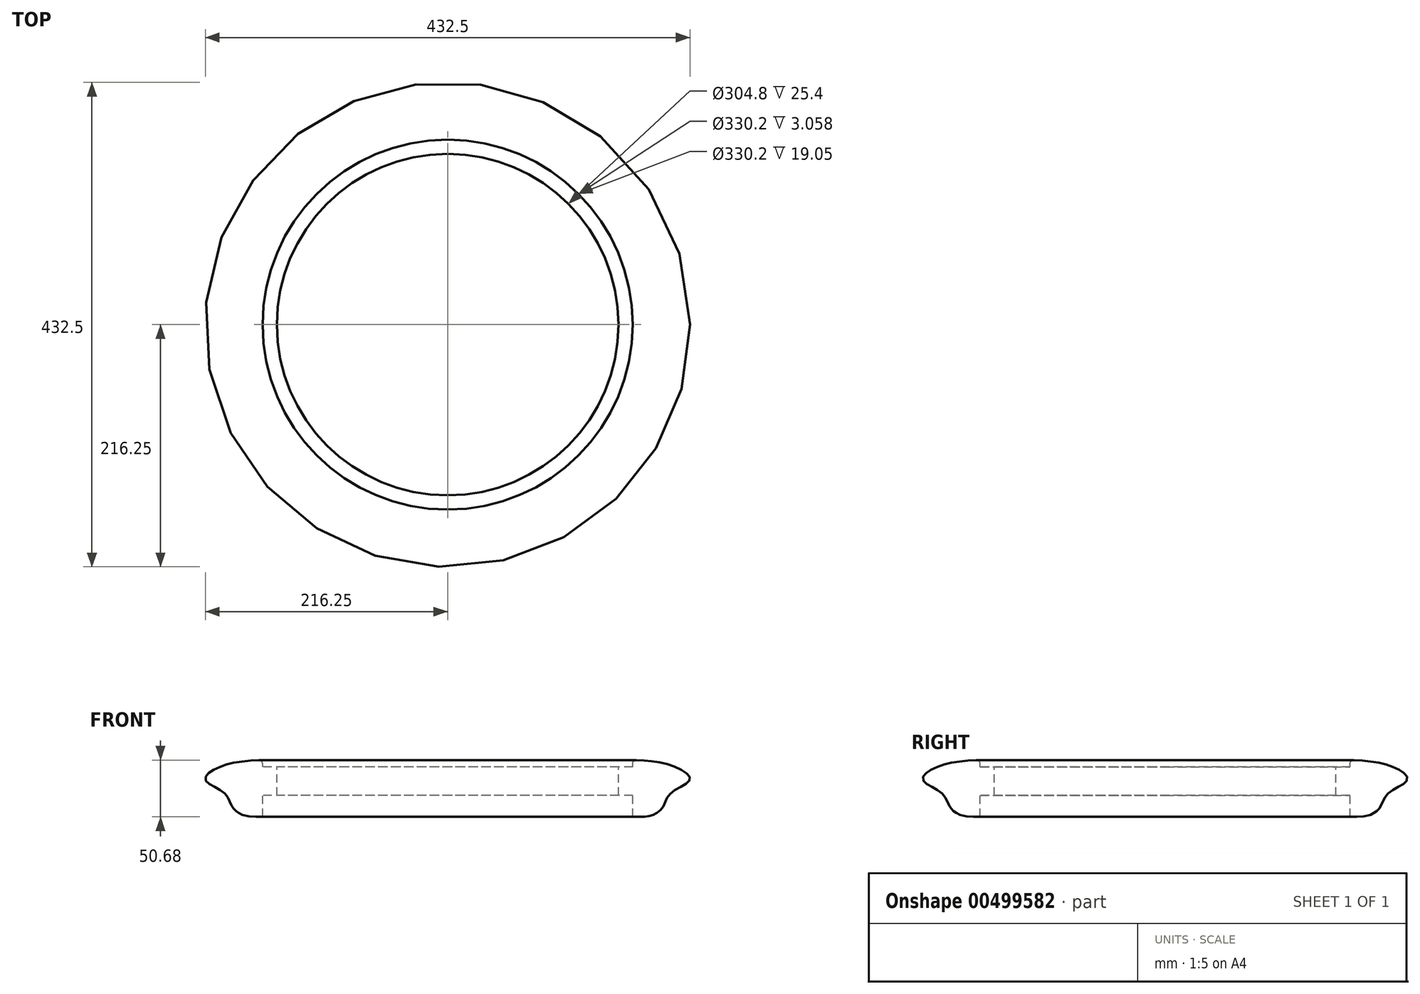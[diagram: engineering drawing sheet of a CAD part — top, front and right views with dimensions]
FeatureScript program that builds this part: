
annotation { "Feature Type Name" : "Feature", "Feature Type Description" : "" }
export const myFeature = defineFeature(function(context is Context, id is Id, definition is map)
    precondition{}
    {
        {
            var Q0;
            Q0=qCreatedBy(makeId("Front.planeOp"),FACE);
            var sketch = newSketch(context, id + "F0", { "sketchPlane" : qUnion([Q0])});
            skLineSegment(sketch, "E0", {"start": v(0, 33.86) * mm, "end": v(0, -42.34) * mm, "construction": true});
            skLineSegment(sketch, "E1", {"start": v(0, 0) * mm, "end": v(-152.4, 0) * mm, "construction": true});
            skSolve(sketch);
        }
        {
            var Q0;
            Q0=qCreatedBy(makeId("Front.planeOp"),FACE);
            var sketch = newSketch(context, id + "F1", { "sketchPlane" : qUnion([Q0])});
            skLineSegment(sketch, "E2", {"start": v(-152.4, 0) * mm, "end": v(-152.4, 25.4) * mm});
            skLineSegment(sketch, "E3", {"start": v(-152.4, 0) * mm, "end": v(-165.1, 0) * mm});
            skLineSegment(sketch, "E4", {"start": v(-152.4, 25.4) * mm, "end": v(-165.1, 25.4) * mm});
            skLineSegment(sketch, "E5", {"start": v(-165.1, 0) * mm, "end": v(-165.1, -19.05) * mm});
            skLineSegment(sketch, "E6", {"start": v(-165.1, 25.4) * mm, "end": v(-165.1, 31.75) * mm});
            skFitSpline(sketch, "E7", {"points": [v(-165.1, -19.05) * mm, v(-182.15, -17.64) * mm, v(-192.02, -10.3) * mm, v(-199.07, 2.01) * mm, v(-216.12, 14.15) * mm, v(-202.18, 25.95) * mm, v(-165.1, 31.75) * mm], "startDerivative": vector(-163.52, 1.27) * mm, "endDerivative": vector(153.64, 4.81) * mm});
            skSolve(sketch);
        }
        {
            var Q0;
            Q0=makeQuery(id+"F1.imprint","IMPRINT",FACE,{"disambiguationData":[TD([[makeQuery(id+"F1.imprint","IMPRINT",EDGE,{"derivedFrom":sQuery(id+"F1.wireOp",EDGE,"E2")}),1.0]])]});
            var Q1;
            Q1=sQuery(id+"F0.wireOp",EDGE,"E0");
            revolve(context, id + "F2", {"entities" : qUnion([Q0]), "axis" : qUnion([Q1]), "revolveType" : RevolveType.FULL});
        }
        {
            var Q0;
            Q0=makeQuery(id+"F2.opRevolve","SWEPT_EDGE",EDGE,{"disambiguationData":[OSD([sQuery(id+"F1.wireOp",EDGE,"E6"),sQuery(id+"F1.wireOp",EDGE,"E7")])]});
            fillet(context, id + "F3", {"entities" : qUnion([Q0]), "radius" : 3.17 * mm, "tangentPropagation" : true, "allowEdgeOverflow" : false});
        }
    });
